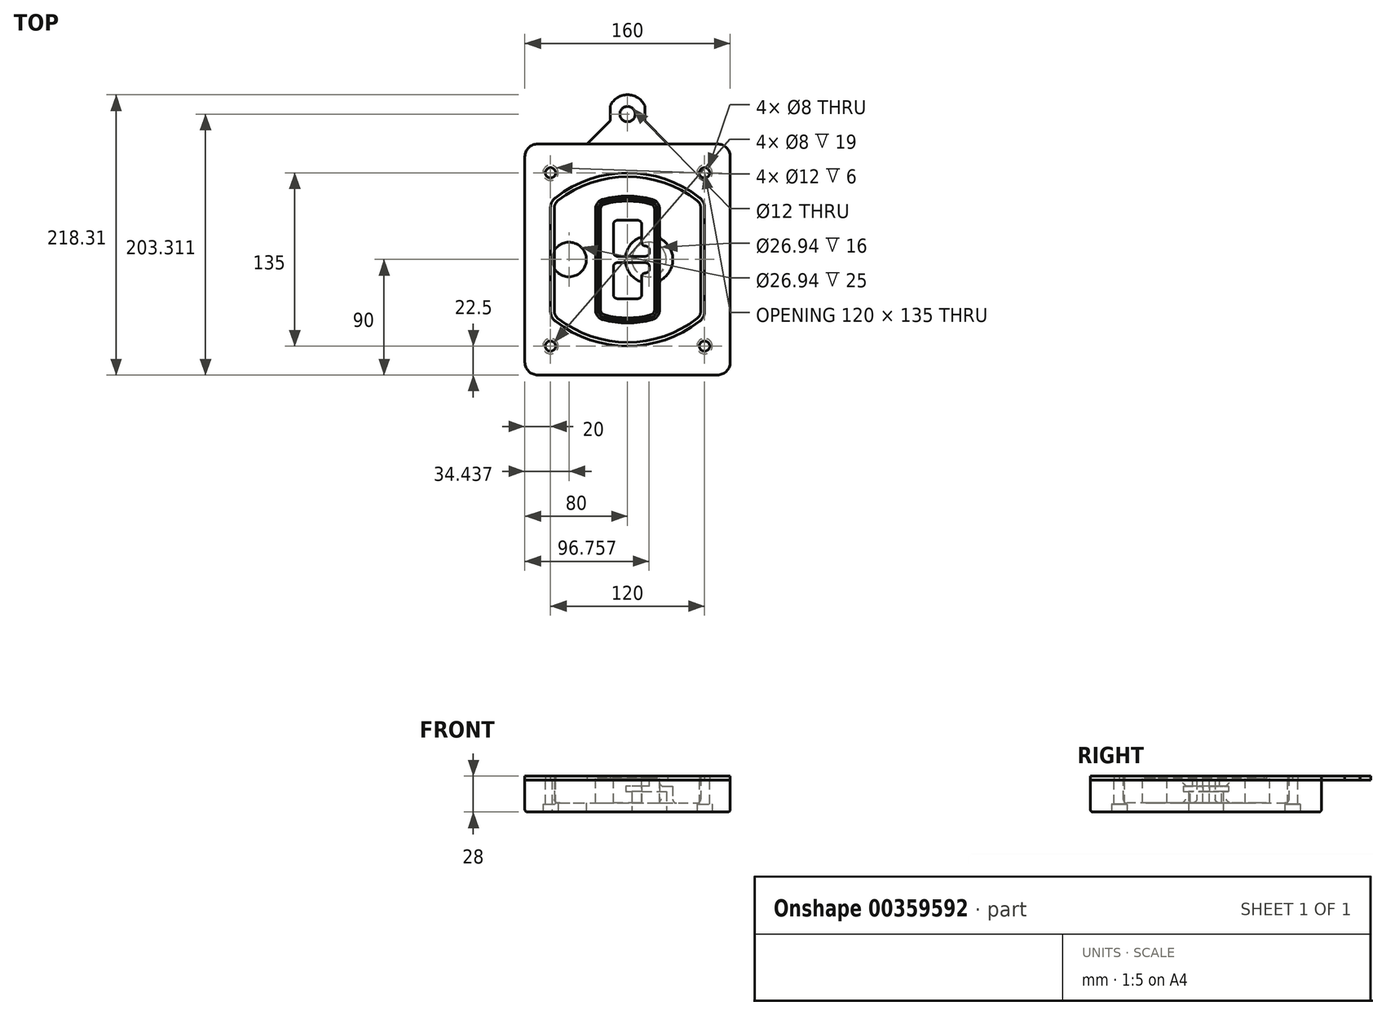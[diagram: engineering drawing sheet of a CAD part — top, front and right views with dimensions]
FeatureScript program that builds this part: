
annotation { "Feature Type Name" : "Feature", "Feature Type Description" : "" }
export const myFeature = defineFeature(function(context is Context, id is Id, definition is map)
    precondition{}
    {
        {
            var Q0;
            Q0=qCreatedBy(makeId("Top.planeOp"),FACE);
            var sketch = newSketch(context, id + "F0", { "sketchPlane" : qUnion([Q0])});
            skPoint(sketch, "E0.rect.middle", {"position": v(0, 0) * mm});
            skLineSegment(sketch, "E1.bottom", {"start": v(-70, -90) * mm, "end": v(70, -90) * mm});
            skLineSegment(sketch, "E1.top", {"start": v(-70, 90) * mm, "end": v(70, 90) * mm});
            skLineSegment(sketch, "E1.left", {"start": v(-80, -80) * mm, "end": v(-80, 80) * mm});
            skLineSegment(sketch, "E1.right", {"start": v(80, -80) * mm, "end": v(80, 80) * mm});
            skLineSegment(sketch, "E2", {"start": v(-80, 90) * mm, "end": v(80, -90) * mm, "construction": true});
            skLineSegment(sketch, "E3", {"start": v(80, 90) * mm, "end": v(-80, -90) * mm, "construction": true});
            skCircle(sketch, "E4", {"center": v(-60, 67.5) * mm, "radius": 4 * mm});
            skCircle(sketch, "E5", {"center": v(60, 67.5) * mm, "radius": 4 * mm});
            skCircle(sketch, "E6", {"center": v(60, -67.5) * mm, "radius": 4 * mm});
            skCircle(sketch, "E7", {"center": v(-60, -67.5) * mm, "radius": 4 * mm});
            skLineSegment(sketch, "E8", {"start": v(-60, 67.5) * mm, "end": v(60, 67.5) * mm, "construction": true});
            skLineSegment(sketch, "E9", {"start": v(60, 67.5) * mm, "end": v(60, -67.5) * mm, "construction": true});
            skLineSegment(sketch, "E10", {"start": v(60, -67.5) * mm, "end": v(-60, -67.5) * mm, "construction": true});
            skLineSegment(sketch, "E11", {"start": v(-60, -67.5) * mm, "end": v(-60, 67.5) * mm, "construction": true});
            skLineSegment(sketch, "E12", {"start": v(-60, 40.3) * mm, "end": v(-60, -40.3) * mm});
            skLineSegment(sketch, "E13", {"start": v(60, 40.3) * mm, "end": v(60, -40.3) * mm});
            skArc(sketch, "E14", {"start": v(56.15, 48.18) * mm, "mid": v(0, 67.5) * mm, "end": v(-56.15, 48.18) * mm});
            skArc(sketch, "E15", {"start": v(-56.15, -48.18) * mm, "mid": v(0, -67.5) * mm, "end": v(56.15, -48.18) * mm});
            skLineSegment(sketch, "E16", {"start": v(-60, 0) * mm, "end": v(60, 0) * mm, "construction": true});
            skPoint(sketch, "E17.visualSharp", {"position": v(-60, -45) * mm});
            skArc(sketch, "E17.filletArc", {"start": v(-60, -40.3) * mm, "mid": v(-58.99, -44.68) * mm, "end": v(-56.15, -48.18) * mm});
            skPoint(sketch, "E18.visualSharp", {"position": v(-60, 45) * mm});
            skArc(sketch, "E18.filletArc", {"start": v(-56.15, 48.18) * mm, "mid": v(-58.99, 44.68) * mm, "end": v(-60, 40.3) * mm});
            skPoint(sketch, "E19.visualSharp", {"position": v(60, 45) * mm});
            skArc(sketch, "E19.filletArc", {"start": v(60, 40.3) * mm, "mid": v(58.99, 44.68) * mm, "end": v(56.15, 48.18) * mm});
            skPoint(sketch, "E20.visualSharp", {"position": v(60, -45) * mm});
            skArc(sketch, "E20.filletArc", {"start": v(56.15, -48.18) * mm, "mid": v(58.99, -44.68) * mm, "end": v(60, -40.3) * mm});
            skPoint(sketch, "E21.visualSharp", {"position": v(-80, 90) * mm});
            skArc(sketch, "E21.filletArc", {"start": v(-70, 90) * mm, "mid": v(-77.07, 87.07) * mm, "end": v(-80, 80) * mm});
            skPoint(sketch, "E22.visualSharp", {"position": v(80, 90) * mm});
            skArc(sketch, "E22.filletArc", {"start": v(80, 80) * mm, "mid": v(77.07, 87.07) * mm, "end": v(70, 90) * mm});
            skPoint(sketch, "E23.visualSharp", {"position": v(80, -90) * mm});
            skArc(sketch, "E23.filletArc", {"start": v(70, -90) * mm, "mid": v(77.07, -87.07) * mm, "end": v(80, -80) * mm});
            skPoint(sketch, "E24.visualSharp", {"position": v(-80, -90) * mm});
            skArc(sketch, "E24.filletArc", {"start": v(-80, -80) * mm, "mid": v(-77.07, -87.07) * mm, "end": v(-70, -90) * mm});
            skArc(sketch, "E25.0", {"start": v(57, 40.3) * mm, "mid": v(56.3, 43.36) * mm, "end": v(54.3, 45.81) * mm});
            skLineSegment(sketch, "E25.1", {"start": v(57, 40.3) * mm, "end": v(57, -40.3) * mm});
            skArc(sketch, "E25.2", {"start": v(54.3, -45.81) * mm, "mid": v(56.3, -43.36) * mm, "end": v(57, -40.3) * mm});
            skArc(sketch, "E25.3", {"start": v(-54.3, -45.81) * mm, "mid": v(0, -64.5) * mm, "end": v(54.3, -45.81) * mm});
            skArc(sketch, "E25.4", {"start": v(-57, -40.3) * mm, "mid": v(-56.3, -43.36) * mm, "end": v(-54.3, -45.81) * mm});
            skArc(sketch, "E25.5", {"start": v(54.3, 45.81) * mm, "mid": v(0, 64.5) * mm, "end": v(-54.3, 45.81) * mm});
            skLineSegment(sketch, "E25.6", {"start": v(-57, 40.3) * mm, "end": v(-57, -40.3) * mm});
            skArc(sketch, "E25.7", {"start": v(-54.3, 45.81) * mm, "mid": v(-56.3, 43.36) * mm, "end": v(-57, 40.3) * mm});
            skArc(sketch, "E26.0", {"start": v(-58.62, 51.33) * mm, "mid": v(-62.58, 46.43) * mm, "end": v(-64, 40.3) * mm});
            skArc(sketch, "E26.1", {"start": v(58.62, 51.33) * mm, "mid": v(0, 71.5) * mm, "end": v(-58.62, 51.33) * mm});
            skArc(sketch, "E26.2", {"start": v(64, 40.3) * mm, "mid": v(62.58, 46.43) * mm, "end": v(58.62, 51.33) * mm});
            skLineSegment(sketch, "E26.3", {"start": v(64, 40.3) * mm, "end": v(64, -40.3) * mm});
            skArc(sketch, "E26.4", {"start": v(58.62, -51.33) * mm, "mid": v(62.58, -46.43) * mm, "end": v(64, -40.3) * mm});
            skLineSegment(sketch, "E26.5", {"start": v(-64, 40.3) * mm, "end": v(-64, -40.3) * mm});
            skArc(sketch, "E26.6", {"start": v(-58.62, -51.33) * mm, "mid": v(0, -71.5) * mm, "end": v(58.62, -51.33) * mm});
            skArc(sketch, "E26.7", {"start": v(-64, -40.3) * mm, "mid": v(-62.58, -46.43) * mm, "end": v(-58.62, -51.33) * mm});
            skSolve(sketch);
        }
        {
            var Q0;
            Q0=makeQuery(id+"F0.imprint","IMPRINT",FACE,{"disambiguationData":[TD([[makeQuery(id+"F0.imprint","IMPRINT",EDGE,{"derivedFrom":sQuery(id+"F0.wireOp",EDGE,"E1.bottom")}),1.0]])]});
            var Q1;
            Q1=makeQuery(id+"F0.imprint","IMPRINT",FACE,{"disambiguationData":[TD([[makeQuery(id+"F0.imprint","IMPRINT",EDGE,{"derivedFrom":sQuery(id+"F0.wireOp",EDGE,"E12")}),1.0]])]});
            var Q2;
            Q2=makeQuery(id+"F0.imprint","IMPRINT",FACE,{"disambiguationData":[TD([[makeQuery(id+"F0.imprint","IMPRINT",EDGE,{"derivedFrom":sQuery(id+"F0.wireOp",EDGE,"E25.0")}),1.0]])]});
            var Q3;
            Q3=makeQuery(id+"F0.imprint","IMPRINT",FACE,{"disambiguationData":[TD([[makeQuery(id+"F0.imprint","IMPRINT",EDGE,{"derivedFrom":sQuery(id+"F0.wireOp",EDGE,"E12")}),-1.0]])]});
            extrude(context, id + "F1", {"entities" : qUnion([Q0, Q1, Q2, Q3]), "oppositeDirection" : true, "depth" : 25 * mm});
        }
        {
            var Q0;
            Q0=makeQuery(id+"F0.imprint","IMPRINT",FACE,{"disambiguationData":[TD([[makeQuery(id+"F0.imprint","IMPRINT",EDGE,{"derivedFrom":sQuery(id+"F0.wireOp",EDGE,"E12")}),1.0]])]});
            extrude(context, id + "F2", {"entities" : qUnion([Q0]), "operationType" : NewBodyOperationType.ADD, "depth" : 3 * mm});
        }
        {
            var Q0;
            Q0=makeQuery(id+"F0.imprint","IMPRINT",FACE,{"disambiguationData":[TD([[makeQuery(id+"F0.imprint","IMPRINT",EDGE,{"derivedFrom":sQuery(id+"F0.wireOp",EDGE,"E25.0")}),1.0]])]});
            extrude(context, id + "F3", {"entities" : qUnion([Q0]), "operationType" : NewBodyOperationType.REMOVE, "oppositeDirection" : true, "depth" : 18 * mm});
        }
        {
            var Q0;
            Q0=makeQuery(id+"F2.opExtrude","CAP_FACE",FACE,{"disambiguationData":[OSD([sQuery(id+"F0.wireOp",EDGE,"E12"),sQuery(id+"F0.wireOp",EDGE,"E13"),sQuery(id+"F0.wireOp",EDGE,"E14"),sQuery(id+"F0.wireOp",EDGE,"E15"),sQuery(id+"F0.wireOp",EDGE,"E17.filletArc"),sQuery(id+"F0.wireOp",EDGE,"E18.filletArc"),sQuery(id+"F0.wireOp",EDGE,"E19.filletArc"),sQuery(id+"F0.wireOp",EDGE,"E20.filletArc"),sQuery(id+"F0.wireOp",EDGE,"E25.0"),sQuery(id+"F0.wireOp",EDGE,"E25.1"),sQuery(id+"F0.wireOp",EDGE,"E25.2"),sQuery(id+"F0.wireOp",EDGE,"E25.3"),sQuery(id+"F0.wireOp",EDGE,"E25.4"),sQuery(id+"F0.wireOp",EDGE,"E25.5"),sQuery(id+"F0.wireOp",EDGE,"E25.6"),sQuery(id+"F0.wireOp",EDGE,"E25.7")])],"isStart":false});
            var sketch = newSketch(context, id + "F4", { "sketchPlane" : qUnion([Q0])});
            skArc(sketch, "E27.0", {"start": v(-19.08, -46.97) * mm, "mid": v(0, -49.5) * mm, "end": v(19.08, -46.97) * mm});
            skArc(sketch, "E28.0", {"start": v(19.08, 46.97) * mm, "mid": v(0, 49.5) * mm, "end": v(-19.08, 46.97) * mm});
            skLineSegment(sketch, "E29", {"start": v(-25, 39.25) * mm, "end": v(-25, -39.25) * mm});
            skLineSegment(sketch, "E30", {"start": v(25, 39.25) * mm, "end": v(25, -39.25) * mm});
            skLineSegment(sketch, "E31", {"start": v(-25, 45.1) * mm, "end": v(25, 45.1) * mm, "construction": true});
            skLineSegment(sketch, "E32", {"start": v(-25, -45.1) * mm, "end": v(25, -45.1) * mm, "construction": true});
            skPoint(sketch, "E33.visualSharp", {"position": v(-25, 45.1) * mm});
            skArc(sketch, "E33.filletArc", {"start": v(-19.08, 46.97) * mm, "mid": v(-23.35, 44.11) * mm, "end": v(-25, 39.25) * mm});
            skPoint(sketch, "E34.visualSharp", {"position": v(25, 45.1) * mm});
            skArc(sketch, "E34.filletArc", {"start": v(25, 39.25) * mm, "mid": v(23.35, 44.11) * mm, "end": v(19.08, 46.97) * mm});
            skPoint(sketch, "E35.visualSharp", {"position": v(25, -45.1) * mm});
            skArc(sketch, "E35.filletArc", {"start": v(19.08, -46.97) * mm, "mid": v(23.35, -44.11) * mm, "end": v(25, -39.25) * mm});
            skPoint(sketch, "E36.visualSharp", {"position": v(-25, -45.1) * mm});
            skArc(sketch, "E36.filletArc", {"start": v(-25, -39.25) * mm, "mid": v(-23.35, -44.11) * mm, "end": v(-19.08, -46.97) * mm});
            skArc(sketch, "E37.0", {"start": v(54.3, 45.81) * mm, "mid": v(0, 64.5) * mm, "end": v(-54.3, 45.81) * mm});
            skArc(sketch, "E37.1", {"start": v(-54.3, 45.81) * mm, "mid": v(-56.3, 43.36) * mm, "end": v(-57, 40.3) * mm});
            skLineSegment(sketch, "E37.2", {"start": v(-57, 40.3) * mm, "end": v(-57, -40.3) * mm});
            skArc(sketch, "E37.3", {"start": v(-57, -40.3) * mm, "mid": v(-56.3, -43.36) * mm, "end": v(-54.3, -45.81) * mm});
            skArc(sketch, "E37.4", {"start": v(-54.3, -45.81) * mm, "mid": v(0, -64.5) * mm, "end": v(54.3, -45.81) * mm});
            skArc(sketch, "E37.5", {"start": v(54.3, -45.81) * mm, "mid": v(56.3, -43.36) * mm, "end": v(57, -40.3) * mm});
            skLineSegment(sketch, "E37.6", {"start": v(57, 40.3) * mm, "end": v(57, -40.3) * mm});
            skArc(sketch, "E37.7", {"start": v(57, 40.3) * mm, "mid": v(56.3, 43.36) * mm, "end": v(54.3, 45.81) * mm});
            skLineSegment(sketch, "E38.0", {"start": v(23, 39.25) * mm, "end": v(23, -39.25) * mm});
            skArc(sketch, "E38.1", {"start": v(18.56, -45.04) * mm, "mid": v(21.76, -42.9) * mm, "end": v(23, -39.25) * mm});
            skArc(sketch, "E38.2", {"start": v(-18.56, -45.04) * mm, "mid": v(0, -47.5) * mm, "end": v(18.56, -45.04) * mm});
            skArc(sketch, "E38.3", {"start": v(-23, -39.25) * mm, "mid": v(-21.76, -42.9) * mm, "end": v(-18.56, -45.04) * mm});
            skLineSegment(sketch, "E38.4", {"start": v(-23, 39.25) * mm, "end": v(-23, -39.25) * mm});
            skArc(sketch, "E38.5", {"start": v(23, 39.25) * mm, "mid": v(21.76, 42.9) * mm, "end": v(18.56, 45.04) * mm});
            skArc(sketch, "E38.6", {"start": v(-18.56, 45.04) * mm, "mid": v(-21.76, 42.9) * mm, "end": v(-23, 39.25) * mm});
            skArc(sketch, "E38.7", {"start": v(18.56, 45.04) * mm, "mid": v(0, 47.5) * mm, "end": v(-18.56, 45.04) * mm});
            skArc(sketch, "E39.0", {"start": v(21, 39.25) * mm, "mid": v(20.18, 41.68) * mm, "end": v(18.04, 43.1) * mm});
            skLineSegment(sketch, "E39.1", {"start": v(21, 39.25) * mm, "end": v(21, -39.25) * mm});
            skArc(sketch, "E39.2", {"start": v(18.04, -43.1) * mm, "mid": v(20.18, -41.68) * mm, "end": v(21, -39.25) * mm});
            skArc(sketch, "E39.3", {"start": v(-18.04, -43.1) * mm, "mid": v(0, -45.5) * mm, "end": v(18.04, -43.1) * mm});
            skArc(sketch, "E39.4", {"start": v(-21, -39.25) * mm, "mid": v(-20.18, -41.68) * mm, "end": v(-18.04, -43.1) * mm});
            skArc(sketch, "E39.5", {"start": v(18.04, 43.1) * mm, "mid": v(0, 45.5) * mm, "end": v(-18.04, 43.1) * mm});
            skLineSegment(sketch, "E39.6", {"start": v(-21, 39.25) * mm, "end": v(-21, -39.25) * mm});
            skArc(sketch, "E39.7", {"start": v(-18.04, 43.1) * mm, "mid": v(-20.18, 41.68) * mm, "end": v(-21, 39.25) * mm});
            skLineSegment(sketch, "E40", {"start": v(-25, 0) * mm, "end": v(25, 0) * mm, "construction": true});
            skLineSegment(sketch, "E41", {"start": v(-11, 5.5) * mm, "end": v(-11, 27.5) * mm});
            skLineSegment(sketch, "E42", {"start": v(-8, 30.5) * mm, "end": v(8, 30.5) * mm});
            skLineSegment(sketch, "E43", {"start": v(11, 27.5) * mm, "end": v(11, 13.5) * mm});
            skLineSegment(sketch, "E44", {"start": v(14, 10.5) * mm, "end": v(14, 10.5) * mm});
            skLineSegment(sketch, "E45", {"start": v(17, 7.5) * mm, "end": v(17, 5.5) * mm});
            skLineSegment(sketch, "E46", {"start": v(14, 2.5) * mm, "end": v(-8, 2.5) * mm});
            skPoint(sketch, "E47.visualSharp", {"position": v(-11, 30.5) * mm});
            skArc(sketch, "E47.filletArc", {"start": v(-8, 30.5) * mm, "mid": v(-10.12, 29.62) * mm, "end": v(-11, 27.5) * mm});
            skPoint(sketch, "E48.visualSharp", {"position": v(11, 30.5) * mm});
            skArc(sketch, "E48.filletArc", {"start": v(11, 27.5) * mm, "mid": v(10.12, 29.62) * mm, "end": v(8, 30.5) * mm});
            skPoint(sketch, "E49.visualSharp", {"position": v(11, 10.5) * mm});
            skArc(sketch, "E49.filletArc", {"start": v(11, 13.5) * mm, "mid": v(11.88, 11.38) * mm, "end": v(14, 10.5) * mm});
            skPoint(sketch, "E50.visualSharp", {"position": v(17, 10.5) * mm});
            skArc(sketch, "E50.filletArc", {"start": v(17, 7.5) * mm, "mid": v(16.12, 9.62) * mm, "end": v(14, 10.5) * mm});
            skPoint(sketch, "E51.visualSharp", {"position": v(17, 2.5) * mm});
            skArc(sketch, "E51.filletArc", {"start": v(14, 2.5) * mm, "mid": v(16.12, 3.38) * mm, "end": v(17, 5.5) * mm});
            skPoint(sketch, "E52.visualSharp", {"position": v(-11, 2.5) * mm});
            skArc(sketch, "E52.filletArc", {"start": v(-11, 5.5) * mm, "mid": v(-10.12, 3.38) * mm, "end": v(-8, 2.5) * mm});
            skLineSegment(sketch, "E53.0.MirrorCS", {"start": v(14, -2.5) * mm, "end": v(-8, -2.5) * mm});
            skArc(sketch, "E54.0.MirrorCS", {"start": v(-11, -5.5) * mm, "mid": v(-10.12, -3.38) * mm, "end": v(-8, -2.5) * mm});
            skLineSegment(sketch, "E55.0.MirrorCS", {"start": v(-11, -5.5) * mm, "end": v(-11, -27.5) * mm});
            skArc(sketch, "E56.0.MirrorCS", {"start": v(-8, -30.5) * mm, "mid": v(-10.12, -29.62) * mm, "end": v(-11, -27.5) * mm});
            skLineSegment(sketch, "E57.0.MirrorCS", {"start": v(-8, -30.5) * mm, "end": v(8, -30.5) * mm});
            skArc(sketch, "E58.0.MirrorCS", {"start": v(11, -27.5) * mm, "mid": v(10.12, -29.62) * mm, "end": v(8, -30.5) * mm});
            skLineSegment(sketch, "E59.0.MirrorCS", {"start": v(11, -27.5) * mm, "end": v(11, -13.5) * mm});
            skArc(sketch, "E60.0.MirrorCS", {"start": v(11, -13.5) * mm, "mid": v(11.88, -11.38) * mm, "end": v(14, -10.5) * mm});
            skArc(sketch, "E61.0.MirrorCS", {"start": v(17, -7.5) * mm, "mid": v(16.12, -9.62) * mm, "end": v(14, -10.5) * mm});
            skLineSegment(sketch, "E62.0.MirrorCS", {"start": v(17, -7.5) * mm, "end": v(17, -5.5) * mm});
            skArc(sketch, "E63.0.MirrorCS", {"start": v(14, -2.5) * mm, "mid": v(16.12, -3.38) * mm, "end": v(17, -5.5) * mm});
            skSolve(sketch);
        }
        {
            var Q0;
            Q0=makeQuery(id+"F4.imprint","IMPRINT",FACE,{"disambiguationData":[TD([[makeQuery(id+"F4.imprint","IMPRINT",EDGE,{"derivedFrom":sQuery(id+"F4.wireOp",EDGE,"E27.0")}),1.0]])]});
            var Q1;
            Q1=makeQuery(id+"F4.imprint","IMPRINT",FACE,{"disambiguationData":[TD([[makeQuery(id+"F4.imprint","IMPRINT",EDGE,{"derivedFrom":sQuery(id+"F4.wireOp",EDGE,"E38.0")}),-1.0]])]});
            var Q2;
            Q2=makeQuery(id+"F4.imprint","IMPRINT",FACE,{"disambiguationData":[TD([[makeQuery(id+"F4.imprint","IMPRINT",EDGE,{"derivedFrom":sQuery(id+"F4.wireOp",EDGE,"E39.0")}),1.0]])]});
            extrude(context, id + "F5", {"entities" : qUnion([Q0, Q1, Q2]), "operationType" : NewBodyOperationType.ADD, "endBound" : BoundingType.UP_TO_NEXT, "oppositeDirection" : true, "depth" : 25 * mm});
        }
        {
            var Q0;
            Q0=makeQuery(id+"F4.imprint","IMPRINT",FACE,{"disambiguationData":[TD([[makeQuery(id+"F4.imprint","IMPRINT",EDGE,{"derivedFrom":sQuery(id+"F4.wireOp",EDGE,"E38.0")}),-1.0]])]});
            extrude(context, id + "F6", {"entities" : qUnion([Q0]), "operationType" : NewBodyOperationType.REMOVE, "oppositeDirection" : true, "depth" : 2 * mm});
        }
        {
            var Q0;
            Q0=makeQuery(id+"F1.opExtrude","CAP_FACE",FACE,{"disambiguationData":[OSD([sQuery(id+"F0.wireOp",EDGE,"E1.bottom"),sQuery(id+"F0.wireOp",EDGE,"E1.top"),sQuery(id+"F0.wireOp",EDGE,"E1.left"),sQuery(id+"F0.wireOp",EDGE,"E1.right"),sQuery(id+"F0.wireOp",EDGE,"E4"),sQuery(id+"F0.wireOp",EDGE,"E5"),sQuery(id+"F0.wireOp",EDGE,"E6"),sQuery(id+"F0.wireOp",EDGE,"E7"),sQuery(id+"F0.wireOp",EDGE,"E21.filletArc"),sQuery(id+"F0.wireOp",EDGE,"E22.filletArc"),sQuery(id+"F0.wireOp",EDGE,"E23.filletArc"),sQuery(id+"F0.wireOp",EDGE,"E24.filletArc")])],"isStart":false});
            var sketch = newSketch(context, id + "F7", { "sketchPlane" : qUnion([Q0])});
            skCircle(sketch, "E64", {"center": v(16.76, 0) * mm, "radius": 13.47 * mm});
            skCircle(sketch, "E65", {"center": v(-45.56, 0) * mm, "radius": 13.47 * mm});
            skLineSegment(sketch, "E66", {"start": v(80, 0) * mm, "end": v(-80, 0) * mm});
            skCircle(sketch, "E67", {"center": v(16.76, 0) * mm, "radius": 18.47 * mm});
            skCircle(sketch, "E68", {"center": v(60, -67.5) * mm, "radius": 6 * mm});
            skCircle(sketch, "E69", {"center": v(-60, -67.5) * mm, "radius": 6 * mm});
            skCircle(sketch, "E70", {"center": v(-60, 67.5) * mm, "radius": 6 * mm});
            skCircle(sketch, "E71", {"center": v(60, 67.5) * mm, "radius": 6 * mm});
            skSolve(sketch);
        }
        {
            var Q0;
            {var subQ1=sQuery(id+"F7.wireOp",EDGE,"E66");var subQ4=sQuery(id+"F7.wireOp",EDGE,"E64");var subQ6=makeQuery(id+"F7.imprint","INTERSECT",VERTEX,{"disambiguationData":[OD(0.0)],"derivedFrom":[subQ4,subQ1]});Q0=makeQuery(id+"F7.imprint","IMPRINT",FACE,{"disambiguationData":[TD([[makeQuery(id+"F7.imprint","IMPRINT",EDGE,{"disambiguationData":[TD([[subQ6,-1.0]])],"derivedFrom":subQ4}),-1.0]])]});}
            var Q1;
            {var subQ0=sQuery(id+"F7.wireOp",EDGE,"E66");var subQ1=sQuery(id+"F7.wireOp",EDGE,"E64");var subQ3=makeQuery(id+"F7.imprint","INTERSECT",VERTEX,{"disambiguationData":[OD(0.0)],"derivedFrom":[subQ1,subQ0]});Q1=makeQuery(id+"F7.imprint","IMPRINT",FACE,{"disambiguationData":[TD([[makeQuery(id+"F7.imprint","IMPRINT",EDGE,{"disambiguationData":[TD([[subQ3,-1.0]])],"derivedFrom":subQ1}),1.0]])]});}
            var Q2;
            {var subQ0=sQuery(id+"F7.wireOp",EDGE,"E66");var subQ1=sQuery(id+"F7.wireOp",EDGE,"E64");var subQ3=makeQuery(id+"F7.imprint","INTERSECT",VERTEX,{"disambiguationData":[OD(0.0)],"derivedFrom":[subQ1,subQ0]});Q2=makeQuery(id+"F7.imprint","IMPRINT",FACE,{"disambiguationData":[TD([[makeQuery(id+"F7.imprint","IMPRINT",EDGE,{"disambiguationData":[TD([[subQ3,1.0]])],"derivedFrom":subQ1}),1.0]])]});}
            var Q3;
            {var subQ1=sQuery(id+"F7.wireOp",EDGE,"E66");var subQ4=sQuery(id+"F7.wireOp",EDGE,"E64");var subQ6=makeQuery(id+"F7.imprint","INTERSECT",VERTEX,{"disambiguationData":[OD(0.0)],"derivedFrom":[subQ4,subQ1]});Q3=makeQuery(id+"F7.imprint","IMPRINT",FACE,{"disambiguationData":[TD([[makeQuery(id+"F7.imprint","IMPRINT",EDGE,{"disambiguationData":[TD([[subQ6,1.0]])],"derivedFrom":subQ4}),-1.0]])]});}
            extrude(context, id + "F8", {"entities" : qUnion([Q0, Q1, Q2, Q3]), "operationType" : NewBodyOperationType.ADD, "oppositeDirection" : true, "depth" : 20 * mm});
        }
        {
            var Q0;
            {var subQ0=sQuery(id+"F7.wireOp",EDGE,"E66");var subQ1=sQuery(id+"F7.wireOp",EDGE,"E64");var subQ3=makeQuery(id+"F7.imprint","INTERSECT",VERTEX,{"disambiguationData":[OD(0.0)],"derivedFrom":[subQ1,subQ0]});Q0=makeQuery(id+"F7.imprint","IMPRINT",FACE,{"disambiguationData":[TD([[makeQuery(id+"F7.imprint","IMPRINT",EDGE,{"disambiguationData":[TD([[subQ3,-1.0]])],"derivedFrom":subQ1}),1.0]])]});}
            var Q1;
            {var subQ0=sQuery(id+"F7.wireOp",EDGE,"E66");var subQ1=sQuery(id+"F7.wireOp",EDGE,"E64");var subQ3=makeQuery(id+"F7.imprint","INTERSECT",VERTEX,{"disambiguationData":[OD(0.0)],"derivedFrom":[subQ1,subQ0]});Q1=makeQuery(id+"F7.imprint","IMPRINT",FACE,{"disambiguationData":[TD([[makeQuery(id+"F7.imprint","IMPRINT",EDGE,{"disambiguationData":[TD([[subQ3,1.0]])],"derivedFrom":subQ1}),1.0]])]});}
            extrude(context, id + "F9", {"entities" : qUnion([Q0, Q1]), "operationType" : NewBodyOperationType.REMOVE, "oppositeDirection" : true, "depth" : 16 * mm});
        }
        {
            var Q0;
            {var subQ0=sQuery(id+"F7.wireOp",EDGE,"E66");var subQ1=sQuery(id+"F7.wireOp",EDGE,"E65");var subQ3=makeQuery(id+"F7.imprint","INTERSECT",VERTEX,{"disambiguationData":[OD(0.0)],"derivedFrom":[subQ1,subQ0]});Q0=makeQuery(id+"F7.imprint","IMPRINT",FACE,{"disambiguationData":[TD([[makeQuery(id+"F7.imprint","IMPRINT",EDGE,{"disambiguationData":[TD([[subQ3,-1.0]])],"derivedFrom":subQ1}),1.0]])]});}
            var Q1;
            {var subQ0=sQuery(id+"F7.wireOp",EDGE,"E66");var subQ1=sQuery(id+"F7.wireOp",EDGE,"E65");var subQ3=makeQuery(id+"F7.imprint","INTERSECT",VERTEX,{"disambiguationData":[OD(0.0)],"derivedFrom":[subQ1,subQ0]});Q1=makeQuery(id+"F7.imprint","IMPRINT",FACE,{"disambiguationData":[TD([[makeQuery(id+"F7.imprint","IMPRINT",EDGE,{"disambiguationData":[TD([[subQ3,1.0]])],"derivedFrom":subQ1}),1.0]])]});}
            extrude(context, id + "F10", {"entities" : qUnion([Q0, Q1]), "operationType" : NewBodyOperationType.REMOVE, "oppositeDirection" : true, "depth" : 25 * mm});
        }
        {
            var Q0;
            Q0=makeQuery(id+"F7.imprint","IMPRINT",FACE,{"disambiguationData":[TD([[makeQuery(id+"F7.imprint","IMPRINT",EDGE,{"derivedFrom":sQuery(id+"F7.wireOp",EDGE,"E68")}),1.0]])]});
            var Q1;
            Q1=makeQuery(id+"F7.imprint","IMPRINT",FACE,{"disambiguationData":[TD([[makeQuery(id+"F7.imprint","IMPRINT",EDGE,{"derivedFrom":makeQuery(id+"F1.opExtrude","CAP_EDGE",EDGE,{"disambiguationData":[OSD([sQuery(id+"F0.wireOp",EDGE,"E5")])],"isStart":false})}),-1.0]])]});
            var Q2;
            Q2=makeQuery(id+"F7.imprint","IMPRINT",FACE,{"disambiguationData":[TD([[makeQuery(id+"F7.imprint","IMPRINT",EDGE,{"derivedFrom":sQuery(id+"F7.wireOp",EDGE,"E69")}),1.0]])]});
            var Q3;
            Q3=makeQuery(id+"F7.imprint","IMPRINT",FACE,{"disambiguationData":[TD([[makeQuery(id+"F7.imprint","IMPRINT",EDGE,{"derivedFrom":makeQuery(id+"F1.opExtrude","CAP_EDGE",EDGE,{"disambiguationData":[OSD([sQuery(id+"F0.wireOp",EDGE,"E4")])],"isStart":false})}),-1.0]])]});
            var Q4;
            Q4=makeQuery(id+"F7.imprint","IMPRINT",FACE,{"disambiguationData":[TD([[makeQuery(id+"F7.imprint","IMPRINT",EDGE,{"derivedFrom":sQuery(id+"F7.wireOp",EDGE,"E70")}),1.0]])]});
            var Q5;
            Q5=makeQuery(id+"F7.imprint","IMPRINT",FACE,{"disambiguationData":[TD([[makeQuery(id+"F7.imprint","IMPRINT",EDGE,{"derivedFrom":makeQuery(id+"F1.opExtrude","CAP_EDGE",EDGE,{"disambiguationData":[OSD([sQuery(id+"F0.wireOp",EDGE,"E7")])],"isStart":false})}),-1.0]])]});
            var Q6;
            Q6=makeQuery(id+"F7.imprint","IMPRINT",FACE,{"disambiguationData":[TD([[makeQuery(id+"F7.imprint","IMPRINT",EDGE,{"derivedFrom":sQuery(id+"F7.wireOp",EDGE,"E71")}),1.0]])]});
            var Q7;
            Q7=makeQuery(id+"F7.imprint","IMPRINT",FACE,{"disambiguationData":[TD([[makeQuery(id+"F7.imprint","IMPRINT",EDGE,{"derivedFrom":makeQuery(id+"F1.opExtrude","CAP_EDGE",EDGE,{"disambiguationData":[OSD([sQuery(id+"F0.wireOp",EDGE,"E6")])],"isStart":false})}),-1.0]])]});
            extrude(context, id + "F11", {"entities" : qUnion([Q0, Q1, Q2, Q3, Q4, Q5, Q6, Q7]), "operationType" : NewBodyOperationType.REMOVE, "oppositeDirection" : true, "depth" : 6 * mm});
        }
        {
            var Q0;
            Q0=makeQuery(id+"F9.boolean.opBoolean","COPY",FACE,{"derivedFrom":makeQuery(id+"F9.opExtrude","CAP_FACE",FACE,{"disambiguationData":[OSD([sQuery(id+"F7.wireOp",EDGE,"E64")])],"isStart":false})});
            var sketch = newSketch(context, id + "F12", { "sketchPlane" : qUnion([Q0])});
            skArc(sketch, "E72.0", {"start": v(11, 17.55) * mm, "mid": v(2.57, 11.82) * mm, "end": v(-1.54, 2.5) * mm});
            skArc(sketch, "E72.1", {"start": v(-1.54, -2.5) * mm, "mid": v(2.57, -11.82) * mm, "end": v(11, -17.55) * mm});
            skLineSegment(sketch, "E73", {"start": v(-1.54, -2.5) * mm, "end": v(14, -2.5) * mm});
            skLineSegment(sketch, "E74.0", {"start": v(14, 2.5) * mm, "end": v(-1.54, 2.5) * mm});
            skArc(sketch, "E74.1", {"start": v(14, 2.5) * mm, "mid": v(16.12, 3.38) * mm, "end": v(17, 5.5) * mm});
            skLineSegment(sketch, "E74.2", {"start": v(17, 7.5) * mm, "end": v(17, 5.5) * mm});
            skArc(sketch, "E74.3", {"start": v(17, 7.5) * mm, "mid": v(16.12, 9.62) * mm, "end": v(14, 10.5) * mm});
            skArc(sketch, "E74.4", {"start": v(11, 13.5) * mm, "mid": v(11.88, 11.38) * mm, "end": v(14, 10.5) * mm});
            skLineSegment(sketch, "E74.5", {"start": v(11, 17.55) * mm, "end": v(11, 13.5) * mm});
            skLineSegment(sketch, "E74.7", {"start": v(14, -2.5) * mm, "end": v(-1.54, -2.5) * mm});
            skArc(sketch, "E74.8", {"start": v(14, -2.5) * mm, "mid": v(16.12, -3.38) * mm, "end": v(17, -5.5) * mm});
            skLineSegment(sketch, "E74.9", {"start": v(17, -7.5) * mm, "end": v(17, -5.5) * mm});
            skArc(sketch, "E74.10", {"start": v(17, -7.5) * mm, "mid": v(16.12, -9.62) * mm, "end": v(14, -10.5) * mm});
            skArc(sketch, "E74.11", {"start": v(11, -13.5) * mm, "mid": v(11.88, -11.38) * mm, "end": v(14, -10.5) * mm});
            skLineSegment(sketch, "E74.12", {"start": v(11, -17.55) * mm, "end": v(11, -13.5) * mm});
            skPoint(sketch, "E75.orphan", {"position": v(11, -27.5) * mm});
            skPoint(sketch, "E76.orphan", {"position": v(-8, -2.5) * mm});
            skPoint(sketch, "E77.orphan", {"position": v(-8, 2.5) * mm});
            skPoint(sketch, "E78.orphan", {"position": v(11, 27.5) * mm});
            skSolve(sketch);
        }
        {
            var Q0;
            {var subQ7=sQuery(id+"F12.wireOp",EDGE,"E72.0");var subQ14=sQuery(id+"F12.wireOp",EDGE,"E72.1");var subQ16=sQuery(id+"F12.wireOp",EDGE,"E74.1");var subQ18=sQuery(id+"F12.wireOp",EDGE,"E74.8");Q0=qUnion([makeQuery(id+"F12.imprint","IMPRINT",FACE,{"disambiguationData":[TD([[makeQuery(id+"F12.imprint","IMPRINT",EDGE,{"derivedFrom":subQ7}),1.0]])]}),makeQuery(id+"F12.imprint","IMPRINT",FACE,{"disambiguationData":[TD([[makeQuery(id+"F12.imprint","IMPRINT",EDGE,{"derivedFrom":subQ14}),1.0]])]}),makeQuery(id+"F12.imprint","IMPRINT",FACE,{"disambiguationData":[TD([[makeQuery(id+"F12.imprint","IMPRINT",EDGE,{"derivedFrom":subQ16}),1.0]])]}),makeQuery(id+"F12.imprint","IMPRINT",FACE,{"disambiguationData":[TD([[makeQuery(id+"F12.imprint","IMPRINT",EDGE,{"derivedFrom":subQ18}),-1.0]])]})]);}
            var Q1;
            Q1=makeQuery(id+"F5.boolean.opBoolean","SPLIT",FACE,{"disambiguationData":[TD([makeQuery(id+"F5.opExtrude","SWEPT_FACE",FACE,{"disambiguationData":[OSD([sQuery(id+"F4.wireOp",EDGE,"E41")])]})])],"derivedFrom":makeQuery(id+"F3.boolean.opBoolean","COPY",FACE,{"derivedFrom":makeQuery(id+"F3.opExtrude","CAP_FACE",FACE,{"disambiguationData":[OSD([sQuery(id+"F0.wireOp",EDGE,"E25.0"),sQuery(id+"F0.wireOp",EDGE,"E25.1"),sQuery(id+"F0.wireOp",EDGE,"E25.2"),sQuery(id+"F0.wireOp",EDGE,"E25.3"),sQuery(id+"F0.wireOp",EDGE,"E25.4"),sQuery(id+"F0.wireOp",EDGE,"E25.5"),sQuery(id+"F0.wireOp",EDGE,"E25.6"),sQuery(id+"F0.wireOp",EDGE,"E25.7")])],"isStart":false})})});
            extrude(context, id + "F13", {"entities" : qUnion([Q0]), "operationType" : NewBodyOperationType.REMOVE, "endBound" : BoundingType.UP_TO_SURFACE, "endBoundEntityFace" : qUnion([Q1]), "depth" : 25 * mm});
        }
        {
            var Q0;
            Q0=makeQuery(id+"F3.boolean.opBoolean","COPY",EDGE,{"derivedFrom":makeQuery(id+"F3.opExtrude","CAP_EDGE",EDGE,{"disambiguationData":[OSD([sQuery(id+"F0.wireOp",EDGE,"E25.6")])],"isStart":false})});
            var Q1;
            Q1=makeQuery(id+"F8.boolean.opBoolean","INTERSECT",EDGE,{"derivedFrom":[makeQuery(id+"F5.opExtrude","SWEPT_FACE",FACE,{"disambiguationData":[OSD([sQuery(id+"F4.wireOp",EDGE,"E30")])]}),makeQuery(id+"F8.opExtrude","CAP_FACE",FACE,{"disambiguationData":[OSD([sQuery(id+"F7.wireOp",EDGE,"E67")])],"isStart":false})]});
            var Q2;
            Q2=makeQuery(id+"F8.boolean.opBoolean","INTERSECT",EDGE,{"disambiguationData":[OD(1.0)],"derivedFrom":[makeQuery(id+"F5.opExtrude","SWEPT_FACE",FACE,{"disambiguationData":[OSD([sQuery(id+"F4.wireOp",EDGE,"E30")])]}),makeQuery(id+"F8.opExtrude","SWEPT_FACE",FACE,{"disambiguationData":[OSD([sQuery(id+"F7.wireOp",EDGE,"E67")])]})]});
            var Q3;
            {var subQ0=makeQuery(id+"F3.boolean.opBoolean","COPY",FACE,{"derivedFrom":makeQuery(id+"F3.opExtrude","CAP_FACE",FACE,{"disambiguationData":[OSD([sQuery(id+"F0.wireOp",EDGE,"E25.0"),sQuery(id+"F0.wireOp",EDGE,"E25.1"),sQuery(id+"F0.wireOp",EDGE,"E25.2"),sQuery(id+"F0.wireOp",EDGE,"E25.3"),sQuery(id+"F0.wireOp",EDGE,"E25.4"),sQuery(id+"F0.wireOp",EDGE,"E25.5"),sQuery(id+"F0.wireOp",EDGE,"E25.6"),sQuery(id+"F0.wireOp",EDGE,"E25.7")])],"isStart":false})});var subQ1=sQuery(id+"F4.wireOp",EDGE,"E30");Q3=makeQuery(id+"F8.boolean.opBoolean","SPLIT",EDGE,{"disambiguationData":[TD([makeQuery(id+"F5.opExtrude","SWEPT_FACE",FACE,{"disambiguationData":[OSD([sQuery(id+"F4.wireOp",EDGE,"E35.filletArc")])]})])],"derivedFrom":makeQuery(id+"F5.opExtrude","TWEAK_EDGE",EDGE,{"derivedFrom":[subQ0,makeQuery(id+"F4.imprint","IMPRINT",EDGE,{"derivedFrom":subQ1})]})});}
            var Q4;
            {var subQ0=sQuery(id+"F0.wireOp",EDGE,"E25.0");var subQ1=sQuery(id+"F0.wireOp",EDGE,"E25.1");var subQ2=sQuery(id+"F0.wireOp",EDGE,"E25.2");var subQ3=sQuery(id+"F0.wireOp",EDGE,"E25.3");var subQ4=sQuery(id+"F0.wireOp",EDGE,"E25.4");var subQ5=sQuery(id+"F0.wireOp",EDGE,"E25.5");var subQ6=sQuery(id+"F0.wireOp",EDGE,"E25.6");var subQ7=sQuery(id+"F0.wireOp",EDGE,"E25.7");Q4=makeQuery(id+"F8.boolean.opBoolean","INTERSECT",EDGE,{"derivedFrom":[makeQuery(id+"F5.boolean.opBoolean","SPLIT",FACE,{"disambiguationData":[TD([makeQuery(id+"F2.opExtrude","SWEPT_FACE",FACE,{"disambiguationData":[OSD([subQ0])]})])],"derivedFrom":makeQuery(id+"F3.boolean.opBoolean","COPY",FACE,{"derivedFrom":makeQuery(id+"F3.opExtrude","CAP_FACE",FACE,{"disambiguationData":[OSD([subQ0,subQ1,subQ2,subQ3,subQ4,subQ5,subQ6,subQ7])],"isStart":false})})}),makeQuery(id+"F8.opExtrude","SWEPT_FACE",FACE,{"disambiguationData":[OSD([sQuery(id+"F7.wireOp",EDGE,"E67")])]})]});}
            var Q5;
            Q5=makeQuery(id+"F8.boolean.opBoolean","INTERSECT",EDGE,{"disambiguationData":[OD(0.0)],"derivedFrom":[makeQuery(id+"F5.opExtrude","SWEPT_FACE",FACE,{"disambiguationData":[OSD([sQuery(id+"F4.wireOp",EDGE,"E30")])]}),makeQuery(id+"F8.opExtrude","SWEPT_FACE",FACE,{"disambiguationData":[OSD([sQuery(id+"F7.wireOp",EDGE,"E67")])]})]});
            fillet(context, id + "F14", {"entities" : qUnion([Q0, Q1, Q2, Q3, Q4, Q5]), "radius" : 3 * mm, "tangentPropagation" : true, "allowEdgeOverflow" : false});
        }
        {
            var Q0;
            Q0=makeQuery(id+"F1.opExtrude","CAP_EDGE",EDGE,{"disambiguationData":[OSD([sQuery(id+"F0.wireOp",EDGE,"E1.bottom")])],"isStart":false});
            fillet(context, id + "F15", {"entities" : qUnion([Q0]), "radius" : 2 * mm, "tangentPropagation" : true, "allowEdgeOverflow" : false});
        }
        {
            var Q0;
            {var subQ0=sQuery(id+"F0.wireOp",EDGE,"E21.filletArc");var subQ1=sQuery(id+"F0.wireOp",EDGE,"E7");var subQ2=sQuery(id+"F0.wireOp",EDGE,"E6");var subQ3=sQuery(id+"F0.wireOp",EDGE,"E5");var subQ4=sQuery(id+"F0.wireOp",EDGE,"E4");var subQ5=sQuery(id+"F0.wireOp",EDGE,"E22.filletArc");var subQ6=sQuery(id+"F0.wireOp",EDGE,"E1.bottom");var subQ7=sQuery(id+"F0.wireOp",EDGE,"E1.right");var subQ8=sQuery(id+"F0.wireOp",EDGE,"E1.top");var subQ9=sQuery(id+"F0.wireOp",EDGE,"E1.left");var subQ10=sQuery(id+"F0.wireOp",EDGE,"E23.filletArc");var subQ11=sQuery(id+"F0.wireOp",EDGE,"E24.filletArc");Q0=makeQuery(id+"F2.boolean.opBoolean","SPLIT",FACE,{"disambiguationData":[TD([makeQuery(id+"F1.opExtrude","SWEPT_FACE",FACE,{"disambiguationData":[OSD([subQ6])]})])],"derivedFrom":makeQuery(id+"F1.opExtrude","CAP_FACE",FACE,{"disambiguationData":[OSD([subQ6,subQ8,subQ9,subQ7,subQ4,subQ3,subQ2,subQ1,subQ0,subQ5,subQ10,subQ11])],"isStart":true})});}
            var sketch = newSketch(context, id + "F16", { "sketchPlane" : qUnion([Q0])});
            skLineSegment(sketch, "E79", {"start": v(0, 90) * mm, "end": v(0, 113.31) * mm, "construction": true});
            skCircle(sketch, "E80", {"center": v(0, 113.31) * mm, "radius": 6 * mm});
            skArc(sketch, "E81", {"start": v(13.43, 120) * mm, "mid": v(0, 128.31) * mm, "end": v(-13.43, 120) * mm});
            skLineSegment(sketch, "E82", {"start": v(-13.43, 120) * mm, "end": v(-13.43, 108) * mm});
            skLineSegment(sketch, "E83", {"start": v(-13.43, 108) * mm, "end": v(-31.43, 90) * mm});
            skLineSegment(sketch, "E84", {"start": v(13.43, 120) * mm, "end": v(13.43, 108) * mm});
            skLineSegment(sketch, "E85", {"start": v(13.43, 108) * mm, "end": v(31.43, 90) * mm});
            skLineSegment(sketch, "E86", {"start": v(-80, 0) * mm, "end": v(80, 0) * mm, "construction": true});
            skArc(sketch, "E87.MirrorCS", {"start": v(-13.43, 120) * mm, "mid": v(0, 128.31) * mm, "end": v(13.43, 120) * mm});
            skLineSegment(sketch, "E88.MirrorCS", {"start": v(80, 0) * mm, "end": v(-80, 0) * mm, "construction": true});
            skLineSegment(sketch, "E89.MirrorCS", {"start": v(13.43, -120) * mm, "end": v(13.43, -108) * mm});
            skLineSegment(sketch, "E90.MirrorCS", {"start": v(-13.43, -120) * mm, "end": v(-13.43, -108) * mm});
            skCircle(sketch, "E91.MirrorC", {"center": v(0, -113.31) * mm, "radius": 6 * mm});
            skArc(sketch, "E92.MirrorCS", {"start": v(-13.43, -120) * mm, "mid": v(0, -128.31) * mm, "end": v(13.43, -120) * mm});
            skArc(sketch, "E93.MirrorCS", {"start": v(13.43, -120) * mm, "mid": v(0, -128.31) * mm, "end": v(-13.43, -120) * mm});
            skLineSegment(sketch, "E94.MirrorCS", {"start": v(13.43, -108) * mm, "end": v(31.43, -90) * mm});
            skLineSegment(sketch, "E95.MirrorCS", {"start": v(-13.43, -108) * mm, "end": v(-31.43, -90) * mm});
            skLineSegment(sketch, "E96.MirrorCS", {"start": v(0, -90) * mm, "end": v(0, -113.31) * mm, "construction": true});
            skSolve(sketch);
        }
        {
            var Q0;
            Q0=makeQuery(id+"F16.imprint","IMPRINT",FACE,{"disambiguationData":[TD([[makeQuery(id+"F16.imprint","IMPRINT",EDGE,{"derivedFrom":sQuery(id+"F16.wireOp",EDGE,"E82")}),1.0]])]});
            var Q1;
            Q1=makeQuery(id+"F16.imprint","IMPRINT",FACE,{"disambiguationData":[TD([[makeQuery(id+"F16.imprint","IMPRINT",EDGE,{"derivedFrom":sQuery(id+"F16.wireOp",EDGE,"E89.MirrorCS")}),1.0]])]});
            var Q2;
            Q2=makeQuery(id+"F2.opExtrude","CAP_FACE",FACE,{"disambiguationData":[OSD([sQuery(id+"F0.wireOp",EDGE,"E12"),sQuery(id+"F0.wireOp",EDGE,"E13"),sQuery(id+"F0.wireOp",EDGE,"E14"),sQuery(id+"F0.wireOp",EDGE,"E15"),sQuery(id+"F0.wireOp",EDGE,"E17.filletArc"),sQuery(id+"F0.wireOp",EDGE,"E18.filletArc"),sQuery(id+"F0.wireOp",EDGE,"E19.filletArc"),sQuery(id+"F0.wireOp",EDGE,"E20.filletArc"),sQuery(id+"F0.wireOp",EDGE,"E25.0"),sQuery(id+"F0.wireOp",EDGE,"E25.1"),sQuery(id+"F0.wireOp",EDGE,"E25.2"),sQuery(id+"F0.wireOp",EDGE,"E25.3"),sQuery(id+"F0.wireOp",EDGE,"E25.4"),sQuery(id+"F0.wireOp",EDGE,"E25.5"),sQuery(id+"F0.wireOp",EDGE,"E25.6"),sQuery(id+"F0.wireOp",EDGE,"E25.7")])],"isStart":false});
            extrude(context, id + "F17", {"entities" : qUnion([Q0, Q1]), "endBound" : BoundingType.UP_TO_SURFACE, "endBoundEntityFace" : qUnion([Q2]), "depth" : 25 * mm});
        }
        {
            var Q0;
            {var subQ0=sQuery(id+"F0.wireOp",EDGE,"E21.filletArc");var subQ1=sQuery(id+"F0.wireOp",EDGE,"E7");var subQ2=sQuery(id+"F0.wireOp",EDGE,"E6");var subQ3=sQuery(id+"F0.wireOp",EDGE,"E5");var subQ4=sQuery(id+"F0.wireOp",EDGE,"E4");var subQ5=sQuery(id+"F0.wireOp",EDGE,"E22.filletArc");var subQ6=sQuery(id+"F0.wireOp",EDGE,"E1.bottom");var subQ7=sQuery(id+"F0.wireOp",EDGE,"E1.right");var subQ8=sQuery(id+"F0.wireOp",EDGE,"E1.top");var subQ9=sQuery(id+"F0.wireOp",EDGE,"E1.left");var subQ10=sQuery(id+"F0.wireOp",EDGE,"E23.filletArc");var subQ11=sQuery(id+"F0.wireOp",EDGE,"E24.filletArc");Q0=makeQuery(id+"F2.boolean.opBoolean","SPLIT",FACE,{"disambiguationData":[TD([makeQuery(id+"F1.opExtrude","SWEPT_FACE",FACE,{"disambiguationData":[OSD([subQ6])]})])],"derivedFrom":makeQuery(id+"F1.opExtrude","CAP_FACE",FACE,{"disambiguationData":[OSD([subQ6,subQ8,subQ9,subQ7,subQ4,subQ3,subQ2,subQ1,subQ0,subQ5,subQ10,subQ11])],"isStart":true})});}
            var Q1;
            Q1=makeQuery(id+"F2.opExtrude","CAP_FACE",FACE,{"disambiguationData":[OSD([sQuery(id+"F0.wireOp",EDGE,"E12"),sQuery(id+"F0.wireOp",EDGE,"E13"),sQuery(id+"F0.wireOp",EDGE,"E14"),sQuery(id+"F0.wireOp",EDGE,"E15"),sQuery(id+"F0.wireOp",EDGE,"E17.filletArc"),sQuery(id+"F0.wireOp",EDGE,"E18.filletArc"),sQuery(id+"F0.wireOp",EDGE,"E19.filletArc"),sQuery(id+"F0.wireOp",EDGE,"E20.filletArc"),sQuery(id+"F0.wireOp",EDGE,"E25.0"),sQuery(id+"F0.wireOp",EDGE,"E25.1"),sQuery(id+"F0.wireOp",EDGE,"E25.2"),sQuery(id+"F0.wireOp",EDGE,"E25.3"),sQuery(id+"F0.wireOp",EDGE,"E25.4"),sQuery(id+"F0.wireOp",EDGE,"E25.5"),sQuery(id+"F0.wireOp",EDGE,"E25.6"),sQuery(id+"F0.wireOp",EDGE,"E25.7")])],"isStart":false});
            extrude(context, id + "F18", {"entities" : qUnion([Q0]), "endBound" : BoundingType.UP_TO_SURFACE, "endBoundEntityFace" : qUnion([Q1]), "depth" : 25 * mm});
        }
    });
